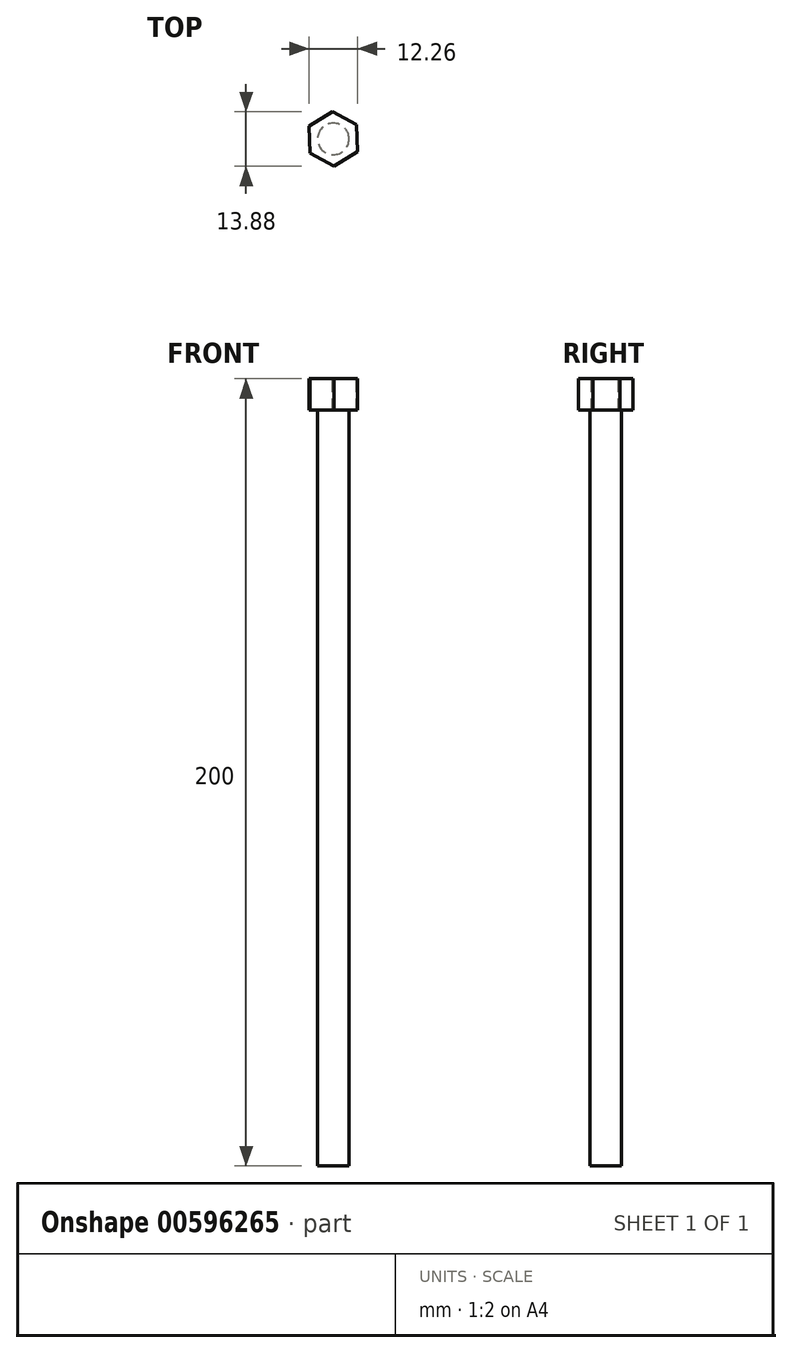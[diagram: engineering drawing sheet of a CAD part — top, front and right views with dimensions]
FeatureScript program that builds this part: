
annotation { "Feature Type Name" : "Feature", "Feature Type Description" : "" }
export const myFeature = defineFeature(function(context is Context, id is Id, definition is map)
    precondition{}
    {
        {
            var Q0;
            Q0=qCreatedBy(makeId("Top.planeOp"),FACE);
            var sketch = newSketch(context, id + "F0", { "sketchPlane" : qUnion([Q0])});
            skCircle(sketch, "E0", {"center": v(0, 0) * mm, "radius": 4 * mm});
            skSolve(sketch);
        }
        {
            var Q0;
            Q0 = qSketchRegion(id + "F0", true);
            extrude(context, id + "F1", {"entities" : qUnion([Q0]), "depth" : 200 * mm, "offsetDistance" : 25 * mm});
        }
        {
            var Q0;
            Q0=makeQuery(id+"F1.opExtrude","CAP_FACE",FACE,{"disambiguationData":[OSD([sQuery(id+"F0.wireOp",EDGE,"E0")])],"isStart":false});
            var sketch = newSketch(context, id + "F2", { "sketchPlane" : qUnion([Q0])});
            skCircle(sketch, "E1.0", {"center": v(0, 0) * mm, "radius": 4 * mm, "construction": true});
            skCircle(sketch, "E2.cCircle", {"center": v(0, 0) * mm, "radius": 6.02 * mm, "construction": true});
            skLineSegment(sketch, "E2.0", {"start": v(-0.23, 6.94) * mm, "end": v(5.9, 3.67) * mm});
            skLineSegment(sketch, "E2.1", {"start": v(5.9, 3.67) * mm, "end": v(6.13, -3.28) * mm});
            skLineSegment(sketch, "E2.2", {"start": v(6.13, -3.28) * mm, "end": v(0.23, -6.94) * mm});
            skLineSegment(sketch, "E2.3", {"start": v(0.23, -6.94) * mm, "end": v(-5.9, -3.67) * mm});
            skLineSegment(sketch, "E2.4", {"start": v(-5.9, -3.67) * mm, "end": v(-6.13, 3.28) * mm});
            skLineSegment(sketch, "E2.5", {"start": v(-6.13, 3.28) * mm, "end": v(-0.23, 6.94) * mm});
            skPoint(sketch, "E2.0.midPoint", {"position": v(2.84, 5.3) * mm});
            skSolve(sketch);
        }
        {
            var Q0;
            Q0 = qSketchRegion(id + "F2", true);
            extrude(context, id + "F3", {"entities" : qUnion([Q0]), "operationType" : NewBodyOperationType.ADD, "oppositeDirection" : true, "depth" : 8 * mm, "offsetDistance" : 25 * mm});
        }
    });
